# Revit family: SoapDish-Vitra-MinimaxSeries-A44777
name_source: partatom
category: Plumbing Fixtures
revit_build: Autodesk Revit 2017 (Build: 20160225_1515(x64)
units: mm (PartAtom-declared; Revit-internal decimal feet)

## family parameters
Cut with Voids When Loaded = No
Host = Face
OmniClass Number = 23.45.00.00
OmniClass Title = Sanitary, Laundry, and Cleaning Equipment
Part Type = Normal
Room Calculation Point = No
Round Connector Dimension = Use Diameter
Shared = Yes

## types (2) — shared parameters
BIMobject category = Sanitary - Bathroom Accessories
Brand = VitrA
CW Connection = No
Coating Material = Chrome
Color = Chrome
Description = Minimax Soap Dish
Design country = Turkey
HW Connection = No
IFC Classification = Sanitary Terminal
Manufacturer = Vitra
Manufacturer name = Vitra
Masterformat 2014 Code = 10 06 20.13
Masterformat 2014 Description = Toilet, Bath, and Laundry Accessory Schedule
Mounting type = Wall Mounted
NBS Referans Code = 35-75-82
NBS Referans Description = Soap Dishes
Nominal Depth (mm) = 111 mm
Nominal Height (mm) = 45 mm  [stored 0.147638 ft]
Nominal Width (mm) = 140 mm  [stored 0.459318 ft]
OmniClass Code = 23-31 25 29 11
OmniClass Description = Hand Soap Holders
Product Type = Soap Dish
Product certification = https://www.vitraglobal.com
Product family = Minimax Series
Product group = Soap Dish
Secondary Material = Glass
UNSPSC Description = Furniture and Furnishings
URL = https://vitraglobal.com
Uniclass 1.4 Code = L8246
Uniclass 1.4 Description = Soap holders/dispensers
Uniclass 2.0 Code = PR-35-75-82
Uniclass 2.0 Description = Soap Dishes
Uniclass 2015 Code = Pr_40_20_76_82
Uniclass 2015 Name = Soap dishes
Uniformat II Code = E20
Uniformat II Description = FURNISHINGS
Vent Connection = No
Waste Connection = No
Youtube = https://www.youtube.com
zero-valued in all types: Default Elevation

## per-type parameters (varying)
| type | Article No. (default) | Model | Product SKU | Product url | Technical description |
| SoapDish-Vitra-MinimaxSeries-A44777 | A44777 | A44777 | A44777 | https://www.vitra.com.tr | https://www.vitra.com.tr |
| SoapDish-Vitra-MinimaxSeries-A44777EXP | A44777EXP | A44777EXP | A44777EXP | https://www.vitraglobal.com | https://www.vitraglobal.com |

note: [stored X ft] marks values corroborated as IEEE doubles in the binary element streams (Revit-internal decimal feet)

## geometry (parser evidence)
native form markers: Sweep x3
no freeform markers — native parametric forms only
